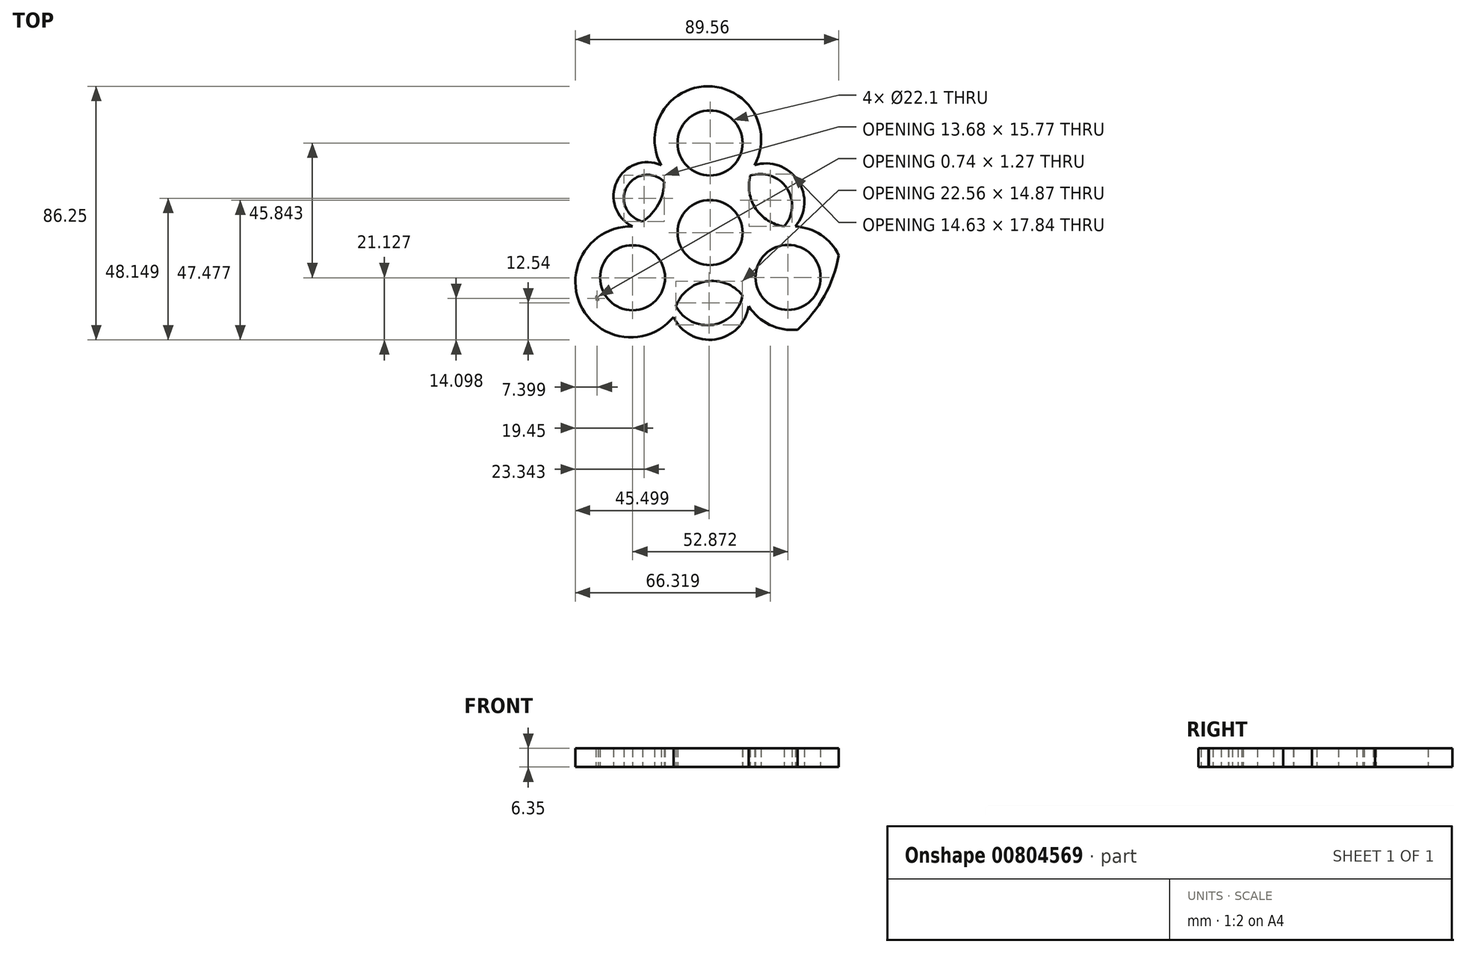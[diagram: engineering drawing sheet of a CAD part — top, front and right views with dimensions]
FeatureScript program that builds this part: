
annotation { "Feature Type Name" : "Feature", "Feature Type Description" : "" }
export const myFeature = defineFeature(function(context is Context, id is Id, definition is map)
    precondition{}
    {
        {
            var Q0;
            Q0=qCreatedBy(makeId("Top.planeOp"),FACE);
            var sketch = newSketch(context, id + "F0", { "sketchPlane" : qUnion([Q0])});
            skCircle(sketch, "E0", {"center": v(0, 0) * mm, "radius": 11.05 * mm});
            skLineSegment(sketch, "E1", {"start": v(0, 0) * mm, "end": v(0, 30.48) * mm});
            skCircle(sketch, "E2", {"center": v(0, 30.48) * mm, "radius": 11.05 * mm});
            skCircle(sketch, "E3.1.0", {"center": v(-26.34, -15.36) * mm, "radius": 11.05 * mm});
            skCircle(sketch, "E3.2.0", {"center": v(26.53, -15.25) * mm, "radius": 11.05 * mm});
            skPoint(sketch, "E3.center", {"position": v(0.06, -0.05) * mm});
            skCircle(sketch, "E4", {"center": v(0, 0) * mm, "radius": 44.45 * mm});
            skCircle(sketch, "E5", {"center": v(-26.34, -15.36) * mm, "radius": 13.97 * mm});
            skCircle(sketch, "E6", {"center": v(26.53, -15.25) * mm, "radius": 13.97 * mm});
            skCircle(sketch, "E7", {"center": v(0, 30.48) * mm, "radius": 13.97 * mm});
            skCircle(sketch, "E8", {"center": v(0.06, -0.05) * mm, "radius": 13.97 * mm});
            skArc(sketch, "E9", {"start": v(15.14, 22.92) * mm, "mid": v(15.54, 8.12) * mm, "end": v(29.05, 2.07) * mm});
            skArc(sketch, "E10", {"start": v(13.13, -25.02) * mm, "mid": v(-1.12, -16.59) * mm, "end": v(-12.37, -28.73) * mm});
            skArc(sketch, "E11", {"start": v(15.14, 22.92) * mm, "mid": v(-0.74, 49.76) * mm, "end": v(-16.63, 22.92) * mm});
            skArc(sketch, "E12", {"start": v(13.13, -25.02) * mm, "mid": v(43.15, -24.44) * mm, "end": v(29.05, 2.07) * mm});
            skArc(sketch, "E13", {"start": v(-26.36, 2.07) * mm, "mid": v(-17.12, 10.46) * mm, "end": v(-16.63, 22.92) * mm});
            skArc(sketch, "E14", {"start": v(-26.36, 2.07) * mm, "mid": v(-44.1, -24.56) * mm, "end": v(-12.37, -28.73) * mm});
            skArc(sketch, "E15", {"start": v(-16.63, 22.92) * mm, "mid": v(-31.75, 17.28) * mm, "end": v(-26.36, 2.07) * mm});
            skArc(sketch, "E16", {"start": v(-15.6, 17.28) * mm, "mid": v(-28.32, 15.43) * mm, "end": v(-22.91, 3.77) * mm});
            skArc(sketch, "E17", {"start": v(-12.37, -28.73) * mm, "mid": v(1.76, -36.35) * mm, "end": v(13.13, -25.02) * mm});
            skArc(sketch, "E18", {"start": v(-11.57, -25.02) * mm, "mid": v(1.06, -31.36) * mm, "end": v(11, -21.3) * mm});
            skArc(sketch, "E19", {"start": v(29.05, 2.07) * mm, "mid": v(29.88, 17.68) * mm, "end": v(15.14, 22.92) * mm});
            skArc(sketch, "E20", {"start": v(25.17, 2.07) * mm, "mid": v(26.06, 15.14) * mm, "end": v(13.65, 19.32) * mm});
            skSolve(sketch);
        }
        {
            var Q0;
            {var subQ0=sQuery(id+"F0.wireOp",EDGE,"E15");Q0=makeQuery(id+"F0.imprint","IMPRINT",FACE,{"disambiguationData":[TD([[makeQuery(id+"F0.imprint","IMPRINT",EDGE,{"derivedFrom":subQ0}),1.0]])]});}
            var Q1;
            Q1=makeQuery(id+"F0.imprint","IMPRINT",FACE,{"disambiguationData":[TD([[makeQuery(id+"F0.imprint","IMPRINT",EDGE,{"derivedFrom":sQuery(id+"F0.wireOp",EDGE,"E0")}),-1.0]])]});
            var Q2;
            Q2=makeQuery(id+"F0.imprint","IMPRINT",FACE,{"disambiguationData":[TD([[makeQuery(id+"F0.imprint","IMPRINT",EDGE,{"derivedFrom":sQuery(id+"F0.wireOp",EDGE,"E8")}),-1.0]])]});
            var Q3;
            {var subQ0=sQuery(id+"F0.wireOp",EDGE,"E4");var subQ1=makeQuery(id+"F0.imprint","INTERSECT",VERTEX,{"derivedFrom":[subQ0,sQuery(id+"F0.wireOp",EDGE,"E7")]});Q3=makeQuery(id+"F0.imprint","IMPRINT",FACE,{"disambiguationData":[TD([[makeQuery(id+"F0.imprint","IMPRINT",EDGE,{"disambiguationData":[TD([[subQ1,1.0]])],"derivedFrom":subQ0}),-1.0]])]});}
            var Q4;
            {var subQ0=sQuery(id+"F0.wireOp",EDGE,"E12");var subQ1=sQuery(id+"F0.wireOp",EDGE,"E4");var subQ2=makeQuery(id+"F0.imprint","INTERSECT",VERTEX,{"disambiguationData":[OD(0.0)],"derivedFrom":[subQ1,subQ0]});Q4=makeQuery(id+"F0.imprint","IMPRINT",FACE,{"disambiguationData":[TD([[makeQuery(id+"F0.imprint","IMPRINT",EDGE,{"disambiguationData":[TD([[subQ2,-1.0]])],"derivedFrom":subQ1}),-1.0]])]});}
            var Q5;
            {var subQ0=sQuery(id+"F0.wireOp",EDGE,"E14");var subQ1=sQuery(id+"F0.wireOp",EDGE,"E4");var subQ2=makeQuery(id+"F0.imprint","INTERSECT",VERTEX,{"disambiguationData":[OD(0.0)],"derivedFrom":[subQ1,subQ0]});Q5=makeQuery(id+"F0.imprint","IMPRINT",FACE,{"disambiguationData":[TD([[makeQuery(id+"F0.imprint","IMPRINT",EDGE,{"disambiguationData":[TD([[subQ2,-1.0]])],"derivedFrom":subQ1}),-1.0]])]});}
            var Q6;
            {var subQ0=sQuery(id+"F0.wireOp",EDGE,"E17");Q6=makeQuery(id+"F0.imprint","IMPRINT",FACE,{"disambiguationData":[TD([[makeQuery(id+"F0.imprint","IMPRINT",EDGE,{"derivedFrom":subQ0}),1.0]])]});}
            var Q7;
            Q7=makeQuery(id+"F0.imprint","IMPRINT",FACE,{"disambiguationData":[TD([[makeQuery(id+"F0.imprint","IMPRINT",EDGE,{"derivedFrom":sQuery(id+"F0.wireOp",EDGE,"E3.1.0")}),-1.0]])]});
            var Q8;
            {var subQ0=sQuery(id+"F0.wireOp",EDGE,"E19");Q8=makeQuery(id+"F0.imprint","IMPRINT",FACE,{"disambiguationData":[TD([[makeQuery(id+"F0.imprint","IMPRINT",EDGE,{"derivedFrom":subQ0}),1.0]])]});}
            var Q9;
            Q9=makeQuery(id+"F0.imprint","IMPRINT",FACE,{"disambiguationData":[TD([[makeQuery(id+"F0.imprint","IMPRINT",EDGE,{"derivedFrom":sQuery(id+"F0.wireOp",EDGE,"E3.2.0")}),-1.0]])]});
            var Q10;
            Q10=makeQuery(id+"F0.imprint","IMPRINT",FACE,{"disambiguationData":[TD([[makeQuery(id+"F0.imprint","IMPRINT",EDGE,{"derivedFrom":sQuery(id+"F0.wireOp",EDGE,"E2")}),-1.0]])]});
            extrude(context, id + "F1", {"entities" : qUnion([Q0, Q1, Q2, Q3, Q4, Q5, Q6, Q7, Q8, Q9, Q10]), "depth" : 6.35 * mm, "offsetDistance" : 25.4 * mm});
        }
    });
